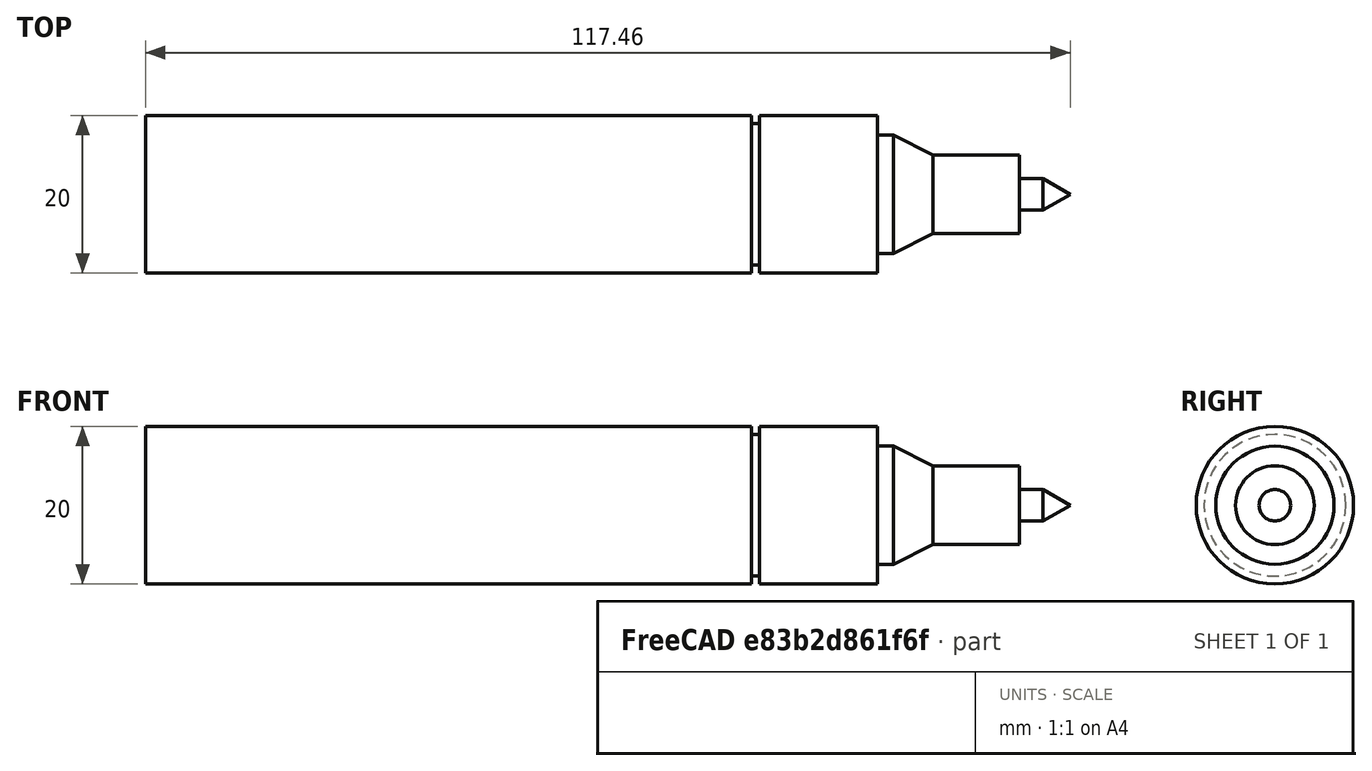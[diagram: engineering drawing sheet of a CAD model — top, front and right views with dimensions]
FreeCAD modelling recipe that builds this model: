
FCSTD DOCUMENT  (FreeCAD 0.18R16131 (Git))
Label: pen_holder_pen
License: All rights reserved
LicenseURL: http://en.wikipedia.org/wiki/All_rights_reserved
objects: Sketcher::SketchObject×1, PartDesign::Revolution×1, PartDesign::Body×1
note: 4 computed .brp shape members not serialized (recipe doc carries the construction recipe); baked Part::Feature solids carry a one-line shape summary decoded from their .brp

FEATURE [Sketcher::SketchObject] Sketch
  MapMode = 5
  Support = -> [XY_Plane]
  sketch-geometry (14):
    g0: LineSegment StartX=0 StartY=0 StartZ=0 EndX=0 EndY=10 EndZ=0
    g1: LineSegment StartX=0 StartY=10 StartZ=0 EndX=77 EndY=10 EndZ=0
    g2: LineSegment StartX=77 StartY=10 StartZ=0 EndX=77 EndY=9 EndZ=0
    g3: LineSegment StartX=77 StartY=9 StartZ=0 EndX=78 EndY=9 EndZ=0
    g4: LineSegment StartX=78 StartY=9 StartZ=0 EndX=78 EndY=10 EndZ=0
    g5: LineSegment StartX=78 StartY=10 StartZ=0 EndX=93 EndY=10 EndZ=0
    g6: LineSegment StartX=93 StartY=10 StartZ=0 EndX=93 EndY=7.5 EndZ=0
    g7: LineSegment StartX=93 StartY=7.5 StartZ=0 EndX=95 EndY=7.5 EndZ=0
    g8: LineSegment StartX=95 StartY=7.5 StartZ=0 EndX=100 EndY=5 EndZ=0
    g9: LineSegment StartX=100 StartY=5 StartZ=0 EndX=111 EndY=5 EndZ=0
    g10: LineSegment StartX=111 StartY=5 StartZ=0 EndX=111 EndY=2 EndZ=0
    g11: LineSegment StartX=111 StartY=2 StartZ=0 EndX=114 EndY=2 EndZ=0
    g12: LineSegment StartX=114 StartY=2 StartZ=0 EndX=117.464 EndY=0 EndZ=0
    g13: LineSegment StartX=117.464 StartY=0 StartZ=0 EndX=0 EndY=0 EndZ=0
  constraints (41):
    c: Coincident(g0,g1)
    c: Coincident(g1,g2)
    c: Coincident(g2,g3)
    c: Coincident(g3,g4)
    c: Coincident(g4,g5)
    c: Coincident(g5,g6)
    c: Coincident(g6,g7)
    c: Coincident(g7,g8)
    c: Coincident(g8,g9)
    c: Coincident(g9,g10)
    c: Coincident(g10,g11)
    c: Coincident(g11,g12)
    c: Coincident(g12,g13)
    c: Horizontal(g1)
    c: Horizontal(g3)
    c: Horizontal(g5)
    c: Horizontal(g7)
    c: Horizontal(g9)
    c: Horizontal(g11)
    c: Horizontal(g13)
    c: Vertical(g10)
    c: Vertical(g6)
    c: Vertical(g4)
    c: Vertical(g2)
    c: Vertical(g0)
    c: Coincident(g0,g13)
    c: Coincident(g-1,g0)
    c: DistanceY(g0,g0) = 10
    c: Horizontal(g1,g4)
    c: DistanceX(g1) = 77
    c: DistanceX(g3,g3) = 1
    c: DistanceY(g4,g4) = 1
    c: DistanceX(g5,g5) = 15
    c: DistanceX(g7,g7) = 2
    c: DistanceY(g12,g7) = 7.5
    c: DistanceY(g12,g9) = 5
    c: DistanceX(g7,g8) = 5
    c: DistanceX(g8,g9) = 11
    c: DistanceX(g11,g11) = 3
    c: DistanceY(g12,g12) = 2
    c: Angle(g12,g13) = 0.523599
FEATURE [PartDesign::Revolution] Revolution
  Angle = 360
  Axis = (1,0,0)
  Base = (0,0,0)
  Profile = -> Sketch
  ReferenceAxis = -> Sketch [H_Axis]
FEATURE [PartDesign::Body] Body
  Group = -> [Sketch,Revolution]
  Origin = -> Origin
  Tip = -> Revolution
